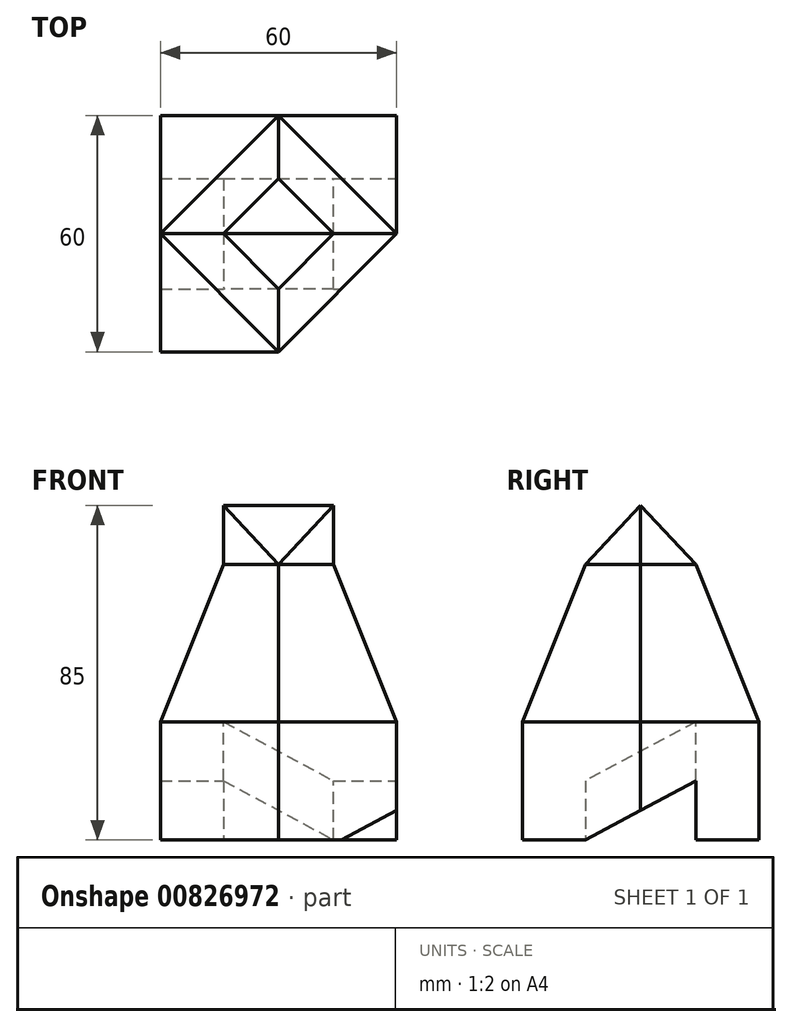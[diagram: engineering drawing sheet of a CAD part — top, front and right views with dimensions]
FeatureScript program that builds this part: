
annotation { "Feature Type Name" : "Feature", "Feature Type Description" : "" }
export const myFeature = defineFeature(function(context is Context, id is Id, definition is map)
    precondition{}
    {
        {
            var Q0;
            Q0=qCreatedBy(makeId("Top.planeOp"),FACE);
            var sketch = newSketch(context, id + "F0", { "sketchPlane" : qUnion([Q0])});
            skLineSegment(sketch, "E0.bottom", {"start": v(30, 30) * mm, "end": v(-30, 30) * mm});
            skLineSegment(sketch, "E0.top", {"start": v(30, -30) * mm, "end": v(-30, -30) * mm});
            skLineSegment(sketch, "E0.left", {"start": v(30, 30) * mm, "end": v(30, -30) * mm});
            skLineSegment(sketch, "E0.right", {"start": v(-30, 30) * mm, "end": v(-30, -30) * mm});
            skPoint(sketch, "E0.middle", {"position": v(0, 0) * mm});
            skSolve(sketch);
        }
        {
            var Q0;
            Q0=makeQuery(id+"F0.imprint","IMPRINT",FACE,{"disambiguationData":[TD([[makeQuery(id+"F0.imprint","IMPRINT",EDGE,{"derivedFrom":sQuery(id+"F0.wireOp",EDGE,"E0.bottom")}),1.0]])]});
            extrude(context, id + "F1", {"entities" : qUnion([Q0]), "depth" : 30 * mm, "offsetDistance" : 25 * mm});
        }
        {
            var Q0;
            Q0=makeQuery(id+"F1.opExtrude","CAP_FACE",FACE,{"disambiguationData":[OSD([sQuery(id+"F0.wireOp",EDGE,"E0.bottom"),sQuery(id+"F0.wireOp",EDGE,"E0.top"),sQuery(id+"F0.wireOp",EDGE,"E0.left"),sQuery(id+"F0.wireOp",EDGE,"E0.right")])],"isStart":false});
            var sketch = newSketch(context, id + "F2", { "sketchPlane" : qUnion([Q0])});
            skLineSegment(sketch, "E1", {"start": v(0, 30) * mm, "end": v(-30, 0) * mm});
            skLineSegment(sketch, "E2", {"start": v(-30, 0) * mm, "end": v(0, -30) * mm});
            skLineSegment(sketch, "E3", {"start": v(0, -30) * mm, "end": v(30, 0) * mm});
            skLineSegment(sketch, "E4", {"start": v(30, 0) * mm, "end": v(0, 30) * mm});
            skSolve(sketch);
        }
        {
            var Q0;
            Q0=makeQuery(id+"F2.imprint","IMPRINT",FACE,{"disambiguationData":[TD([[makeQuery(id+"F2.imprint","IMPRINT",EDGE,{"derivedFrom":sQuery(id+"F2.wireOp",EDGE,"E1")}),1.0]])]});
            cPlane(context, id + "F3", {"entities" : qUnion([Q0]), "cplaneType" : CPlaneType.OFFSET, "offset" : 40 * mm, "width" : 150 * mm, "height" : 150 * mm});
        }
        {
            var Q0;
            Q0=qCreatedBy(id+"F3.planeOp",FACE);
            var sketch = newSketch(context, id + "F4", { "sketchPlane" : qUnion([Q0])});
            skLineSegment(sketch, "E5", {"start": v(0, 14) * mm, "end": v(-14, 0) * mm});
            skLineSegment(sketch, "E6", {"start": v(-14, 0) * mm, "end": v(0, -14) * mm});
            skLineSegment(sketch, "E7", {"start": v(0, -14) * mm, "end": v(14, 0) * mm});
            skLineSegment(sketch, "E8", {"start": v(14, 0) * mm, "end": v(0, 14) * mm});
            skSolve(sketch);
        }
        {
            var Q1;
            Q1=makeQuery(id+"F2.imprint","IMPRINT",FACE,{"disambiguationData":[TD([[makeQuery(id+"F2.imprint","IMPRINT",EDGE,{"derivedFrom":sQuery(id+"F2.wireOp",EDGE,"E1")}),1.0]])]});
            var Q2;
            Q2=makeQuery(id+"F4.imprint","IMPRINT",FACE,{"disambiguationData":[TD([[makeQuery(id+"F4.imprint","IMPRINT",EDGE,{"derivedFrom":sQuery(id+"F4.wireOp",EDGE,"E5")}),1.0]])]});
            loft(context, id + "F5", {"operationType" : NewBodyOperationType.ADD, "sheetProfilesArray" : [{ "sheetProfileEntities" : qUnion([Q1]) }, { "sheetProfileEntities" : qUnion([Q2]) }]});
        }
        {
            var Q0;
            Q0=makeQuery(id+"F5.opLoft","CAP_FACE",FACE,{"disambiguationData":[OSD([makeQuery(id+"F4.imprint","IMPRINT",FACE,{"disambiguationData":[TD([[makeQuery(id+"F4.imprint","IMPRINT",EDGE,{"derivedFrom":sQuery(id+"F4.wireOp",EDGE,"E5")}),1.0]])]})])],"isStart":true});
            extrude(context, id + "F6", {"entities" : qUnion([Q0]), "operationType" : NewBodyOperationType.ADD, "depth" : (85 - 40 - 30) * mm, "offsetDistance" : 25 * mm});
        }
        {
            var Q0;
            Q0=qCreatedBy(makeId("Right.planeOp"),FACE);
            var sketch = newSketch(context, id + "F7", { "sketchPlane" : qUnion([Q0])});
            skLineSegment(sketch, "E9.0", {"start": v(-14, 85) * mm, "end": v(0, 85) * mm});
            skLineSegment(sketch, "E10.0", {"start": v(0, 85) * mm, "end": v(14, 85) * mm});
            skLineSegment(sketch, "E11.0", {"start": v(-14, 85) * mm, "end": v(-14, 70) * mm});
            skLineSegment(sketch, "E12.0", {"start": v(14, 85) * mm, "end": v(14, 70) * mm});
            skLineSegment(sketch, "E13", {"start": v(-14, 70) * mm, "end": v(0, 85) * mm});
            skLineSegment(sketch, "E14", {"start": v(0, 85) * mm, "end": v(14, 70) * mm});
            skSolve(sketch);
        }
        {
            var Q0;
            Q0 = qSketchRegion(id + "F7", true);
            extrude(context, id + "F8", {"entities" : qUnion([Q0]), "operationType" : NewBodyOperationType.REMOVE, "endBound" : BoundingType.UP_TO_NEXT, "oppositeDirection" : true, "depth" : 25 * mm, "offsetDistance" : 25 * mm, "hasSecondDirection" : true, "secondDirectionBound" : SecondDirectionBoundingType.UP_TO_NEXT, "secondDirectionOppositeDirection" : false, "secondDirectionDepth" : 25 * mm});
        }
        {
            var Q0;
            {var subQ0=sQuery(id+"F0.wireOp",EDGE,"E0.left");var subQ1=sQuery(id+"F4.wireOp",EDGE,"E7");var subQ2=sQuery(id+"F4.wireOp",EDGE,"E6");var subQ3=sQuery(id+"F4.wireOp",EDGE,"E5");var subQ4=sQuery(id+"F2.wireOp",EDGE,"E3");var subQ5=sQuery(id+"F2.wireOp",EDGE,"E2");var subQ6=sQuery(id+"F2.wireOp",EDGE,"E1");var subQ7=sQuery(id+"F0.wireOp",EDGE,"E0.right");var subQ8=sQuery(id+"F0.wireOp",EDGE,"E0.top");var subQ9=sQuery(id+"F4.wireOp",EDGE,"E8");var subQ10=sQuery(id+"F2.wireOp",EDGE,"E4");var subQ11=sQuery(id+"F0.wireOp",EDGE,"E0.bottom");var subQ12=makeQuery(id+"F1.opExtrude","CAP_FACE",FACE,{"disambiguationData":[OSD([subQ11,subQ8,subQ0,subQ7])],"isStart":false});Q0=makeQuery(id+"F5.boolean.opBoolean","SPLIT",FACE,{"disambiguationData":[TD([subQ12,makeQuery(id+"F1.opExtrude","SWEPT_FACE",FACE,{"disambiguationData":[OSD([subQ8])]}),makeQuery(id+"F1.opExtrude","SWEPT_FACE",FACE,{"disambiguationData":[OSD([subQ0])]}),makeQuery(id+"F5.opLoft","SWEPT_FACE",FACE,{"disambiguationData":[OSD([subQ11,subQ0,subQ6,subQ4,subQ10,subQ3,subQ1,subQ9])]}),makeQuery(id+"F5.opLoft","SWEPT_FACE",FACE,{"disambiguationData":[OSD([subQ8,subQ7,subQ6,subQ5,subQ4,subQ3,subQ2,subQ1])]}),makeQuery(id+"F5.opLoft","SWEPT_FACE",FACE,{"disambiguationData":[OSD([subQ8,subQ0,subQ5,subQ4,subQ10,subQ2,subQ1,subQ9])]})])],"derivedFrom":subQ12});}
            extrude(context, id + "F9", {"entities" : qUnion([Q0]), "operationType" : NewBodyOperationType.REMOVE, "endBound" : BoundingType.THROUGH_ALL, "oppositeDirection" : true, "depth" : 25 * mm, "offsetDistance" : 25 * mm});
        }
        {
            var Q0;
            Q0=qCreatedBy(makeId("Right.planeOp"),FACE);
            cPlane(context, id + "F10", {"entities" : qUnion([Q0]), "cplaneType" : CPlaneType.OFFSET, "offset" : 14 * mm, "width" : 150 * mm, "height" : 150 * mm});
        }
        {
            var Q0;
            Q0=qCreatedBy(id+"F10.planeOp",FACE);
            var sketch = newSketch(context, id + "F11", { "sketchPlane" : qUnion([Q0])});
            skLineSegment(sketch, "E15", {"start": v(-14, 0) * mm, "end": v(14, 15) * mm});
            skLineSegment(sketch, "E16", {"start": v(14, 15) * mm, "end": v(14, 0) * mm});
            skLineSegment(sketch, "E17", {"start": v(14, 0) * mm, "end": v(-14, 0) * mm, "construction": true});
            skLineSegment(sketch, "E18", {"start": v(-14, 0) * mm, "end": v(-14, -5) * mm});
            skLineSegment(sketch, "E19", {"start": v(-14, -5) * mm, "end": v(14, -5) * mm});
            skLineSegment(sketch, "E20", {"start": v(14, -5) * mm, "end": v(14, 0) * mm});
            skSolve(sketch);
        }
        {
            var Q0;
            Q0=qCreatedBy(makeId("Right.planeOp"),FACE);
            cPlane(context, id + "F12", {"entities" : qUnion([Q0]), "cplaneType" : CPlaneType.OFFSET, "offset" : 14 * mm, "oppositeDirection" : true, "width" : 150 * mm, "height" : 150 * mm});
        }
        {
            var Q0;
            Q0=qCreatedBy(id+"F12.planeOp",FACE);
            var sketch = newSketch(context, id + "F13", { "sketchPlane" : qUnion([Q0])});
            skLineSegment(sketch, "E21", {"start": v(14, 0) * mm, "end": v(14, 30) * mm});
            skLineSegment(sketch, "E22", {"start": v(14, 30) * mm, "end": v(-14, 15) * mm});
            skLineSegment(sketch, "E23", {"start": v(-14, 15) * mm, "end": v(-14, 0) * mm});
            skLineSegment(sketch, "E24", {"start": v(-14, 0) * mm, "end": v(14, 0) * mm, "construction": true});
            skLineSegment(sketch, "E25", {"start": v(-14, 0) * mm, "end": v(-14, -5) * mm});
            skLineSegment(sketch, "E26", {"start": v(-14, -5) * mm, "end": v(14, -5) * mm});
            skLineSegment(sketch, "E27", {"start": v(14, -5) * mm, "end": v(14, 0) * mm});
            skSolve(sketch);
        }
        {
            var Q0;
            Q0=qCreatedBy(makeId("Front.planeOp"),FACE);
            var Q1;
            Q1=sQuery(id+"F13.wireOp",VERTEX,"E23.end");
            cPlane(context, id + "F14", {"entities" : qUnion([Q0, Q1]), "cplaneType" : CPlaneType.PLANE_POINT, "offset" : 25 * mm, "width" : 150 * mm, "height" : 150 * mm});
        }
        {
            var Q0;
            Q0=qCreatedBy(id+"F14.planeOp",FACE);
            var sketch = newSketch(context, id + "F15", { "sketchPlane" : qUnion([Q0])});
            skLineSegment(sketch, "E28", {"start": v(-14, 15) * mm, "end": v(14, 0) * mm});
            skLineSegment(sketch, "E29", {"start": v(-14, 0) * mm, "end": v(14, 0) * mm});
            skLineSegment(sketch, "E30", {"start": v(-14, -5) * mm, "end": v(14, -5) * mm});
            skSolve(sketch);
        }
        {
            var Q0;
            Q0=qCreatedBy(makeId("Front.planeOp"),FACE);
            var Q1;
            Q1=sQuery(id+"F13.wireOp",VERTEX,"E21.start");
            cPlane(context, id + "F16", {"entities" : qUnion([Q0, Q1]), "cplaneType" : CPlaneType.PLANE_POINT, "offset" : 25 * mm, "width" : 150 * mm, "height" : 150 * mm});
        }
        {
            var Q1;
            Q1=makeQuery(id+"F13.imprint","IMPRINT",FACE,{"disambiguationData":[TD([[makeQuery(id+"F13.imprint","IMPRINT",EDGE,{"derivedFrom":sQuery(id+"F13.wireOp",EDGE,"E21")}),1.0]])]});
            var Q2;
            Q2=makeQuery(id+"F11.imprint","IMPRINT",FACE,{"disambiguationData":[TD([[makeQuery(id+"F11.imprint","IMPRINT",EDGE,{"derivedFrom":sQuery(id+"F11.wireOp",EDGE,"E15")}),-1.0]])]});
            var Q3;
            Q3=sQuery(id+"F15.wireOp",EDGE,"E28");
            loft(context, id + "F17", {"operationType" : NewBodyOperationType.REMOVE, "addGuides" : true, "sheetProfilesArray" : [{ "sheetProfileEntities" : qUnion([Q1]) }, { "sheetProfileEntities" : qUnion([Q2]) }], "guidesArray" : [{ "guideEntities" : qUnion([Q3]), "guideDerivativeType" : LoftGuideDerivativeType.DEFAULT, "guideDerivativeMagnitude" : 1 }]});
        }
        {
            var Q0;
            Q0=makeQuery(id+"F1.opExtrude","SWEPT_FACE",FACE,{"disambiguationData":[OSD([sQuery(id+"F0.wireOp",EDGE,"E0.left")])]});
            var sketch = newSketch(context, id + "F18", { "sketchPlane" : qUnion([Q0])});
            skLineSegment(sketch, "E31.0", {"start": v(14, 15) * mm, "end": v(-14, 0) * mm});
            skLineSegment(sketch, "E32.0", {"start": v(14, 0) * mm, "end": v(14, 15) * mm});
            skLineSegment(sketch, "E33.0", {"start": v(-14, 0) * mm, "end": v(14, 0) * mm});
            skSolve(sketch);
        }
        {
            var Q0;
            {var subQ0=sQuery(id+"F18.wireOp",EDGE,"E32.0");Q0=makeQuery(id+"F18.imprint","IMPRINT",FACE,{"disambiguationData":[TD([[makeQuery(id+"F18.imprint","IMPRINT",EDGE,{"derivedFrom":subQ0}),1.0]])]});}
            var Q1;
            {var subQ0=sQuery(id+"F18.wireOp",EDGE,"E33.0");var subQ1=sQuery(id+"F18.wireOp",EDGE,"E31.0");var subQ2=makeQuery(id+"F18.imprint","INTERSECT",VERTEX,{"derivedFrom":[subQ1,subQ0]});Q1=makeQuery(id+"F18.imprint","IMPRINT",FACE,{"disambiguationData":[TD([[makeQuery(id+"F18.imprint","IMPRINT",EDGE,{"disambiguationData":[TD([[subQ2,1.0]])],"derivedFrom":subQ1}),1.0]])]});}
            var Q2;
            Q2=makeQuery(id+"F1.opExtrude","SWEPT_FACE",FACE,{"disambiguationData":[OSD([sQuery(id+"F0.wireOp",EDGE,"E0.right")])]});
            extrude(context, id + "F19", {"entities" : qUnion([Q0, Q1]), "operationType" : NewBodyOperationType.REMOVE, "endBound" : BoundingType.UP_TO_SURFACE, "oppositeDirection" : true, "depth" : 25 * mm, "endBoundEntityFace" : qUnion([Q2]), "offsetDistance" : 25 * mm});
        }
    });
